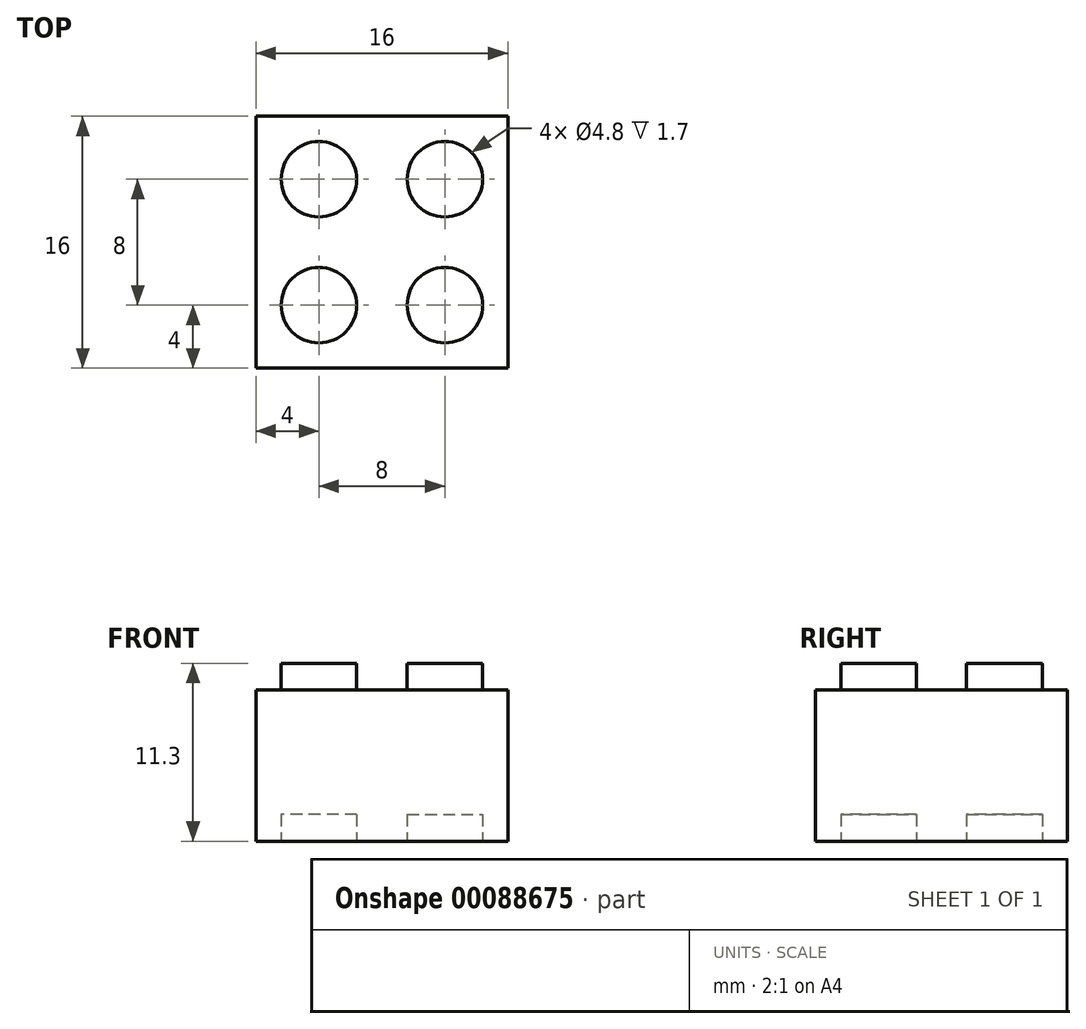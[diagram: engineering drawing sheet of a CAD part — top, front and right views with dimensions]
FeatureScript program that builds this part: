
annotation { "Feature Type Name" : "Feature", "Feature Type Description" : "" }
export const myFeature = defineFeature(function(context is Context, id is Id, definition is map)
    precondition{}
    {
        {
            var Q0;
            Q0=qCreatedBy(makeId("Front.planeOp"),FACE);
            var sketch = newSketch(context, id + "F0", { "sketchPlane" : qUnion([Q0])});
            skLineSegment(sketch, "E0.bottom", {"start": v(-4, 9.6) * mm, "end": v(-2.4, 9.6) * mm});
            skLineSegment(sketch, "E0.top", {"start": v(-4, 0) * mm, "end": v(4, 0) * mm});
            skLineSegment(sketch, "E0.left", {"start": v(-4, 9.6) * mm, "end": v(-4, 0) * mm});
            skLineSegment(sketch, "E0.right", {"start": v(4, 9.6) * mm, "end": v(4, 0) * mm});
            skLineSegment(sketch, "E1.top", {"start": v(-2.4, 11.3) * mm, "end": v(2.4, 11.3) * mm});
            skLineSegment(sketch, "E1.left", {"start": v(-2.4, 9.6) * mm, "end": v(-2.4, 11.3) * mm});
            skLineSegment(sketch, "E1.right", {"start": v(2.4, 9.6) * mm, "end": v(2.4, 11.3) * mm});
            skLineSegment(sketch, "E2", {"start": v(0, 0) * mm, "end": v(0, 24.04) * mm, "construction": true});
            skLineSegment(sketch, "E3.trimOffspring", {"start": v(2.4, 9.6) * mm, "end": v(4, 9.6) * mm});
            skSolve(sketch);
        }
        {
            var Q0;
            Q0=makeQuery(id+"F0.imprint","IMPRINT",FACE,{"disambiguationData":[TD([[makeQuery(id+"F0.imprint","IMPRINT",EDGE,{"derivedFrom":sQuery(id+"F0.wireOp",EDGE,"E0.bottom")}),-1.0]])]});
            extrude(context, id + "F1", {"entities" : qUnion([Q0]), "depth" : 8 * mm});
        }
        {
            var Q0;
            Q0=qCreatedBy(makeId("Top.planeOp"),FACE);
            var Q1;
            Q1=makeQuery(id+"F1.opExtrude","CAP_VERTEX",VERTEX,{"disambiguationData":[OSD([sQuery(id+"F0.wireOp",EDGE,"E1.top"),sQuery(id+"F0.wireOp",EDGE,"E1.right")])],"isStart":true});
            cPlane(context, id + "F2", {"entities" : qUnion([Q0, Q1]), "cplaneType" : CPlaneType.PLANE_POINT, "offset" : 152.4 * mm, "width" : 152.4 * mm, "height" : 152.4 * mm});
        }
        {
            var Q0;
            Q0=qCreatedBy(id+"F2.planeOp",FACE);
            var sketch = newSketch(context, id + "F3", { "sketchPlane" : qUnion([Q0])});
            skLineSegment(sketch, "E4.0", {"start": v(-4, -8) * mm, "end": v(-4, 0) * mm});
            skLineSegment(sketch, "E5.0", {"start": v(4, -8) * mm, "end": v(4, 0) * mm});
            skLineSegment(sketch, "E6", {"start": v(-4, 0) * mm, "end": v(4, 0) * mm});
            skLineSegment(sketch, "E7", {"start": v(-4, -8) * mm, "end": v(4, -8) * mm});
            skLineSegment(sketch, "E8", {"start": v(-4, 0) * mm, "end": v(4, -8) * mm, "construction": true});
            skLineSegment(sketch, "E9", {"start": v(-4, -8) * mm, "end": v(4, 0) * mm, "construction": true});
            skCircle(sketch, "E10", {"center": v(0, -4) * mm, "radius": 2.4 * mm});
            skSolve(sketch);
        }
        {
            var Q0;
            Q0=qSketchRegion(id+"F3",true);
            var Q1;
            Q1=makeQuery(id+"F1.opExtrude","SWEPT_FACE",FACE,{"disambiguationData":[OSD([sQuery(id+"F0.wireOp",EDGE,"E0.bottom")])]});
            extrude(context, id + "F4", {"entities" : qUnion([Q0]), "operationType" : NewBodyOperationType.REMOVE, "endBound" : BoundingType.UP_TO_SURFACE, "oppositeDirection" : true, "endBoundEntityFace" : qUnion([Q1]), "depth" : 25.4 * mm});
        }
        {
            var Q0;
            Q0=qCreatedBy(makeId("Top.planeOp"),FACE);
            var sketch = newSketch(context, id + "F5", { "sketchPlane" : qUnion([Q0])});
            skCircle(sketch, "E11.0", {"center": v(0, -4) * mm, "radius": 2.4 * mm});
            skSolve(sketch);
        }
        {
            var Q0;
            Q0=makeQuery(id+"F5.imprint","IMPRINT",FACE,{"disambiguationData":[TD([[makeQuery(id+"F5.imprint","IMPRINT",EDGE,{"derivedFrom":sQuery(id+"F5.wireOp",EDGE,"E11.0")}),1.0]])]});
            extrude(context, id + "F6", {"entities" : qUnion([Q0]), "operationType" : NewBodyOperationType.REMOVE, "depth" : 1.7 * mm});
        }
        {
            var Q0;
            Q0=qCreatedBy(makeId("Right.planeOp"),FACE);
            var Q1;
            Q1=makeQuery(id+"F1.opExtrude","CAP_VERTEX",VERTEX,{"disambiguationData":[OSD([sQuery(id+"F0.wireOp",EDGE,"E0.right"),sQuery(id+"F0.wireOp",EDGE,"E3.trimOffspring")])],"isStart":false});
            cPlane(context, id + "F7", {"entities" : qUnion([Q0, Q1]), "cplaneType" : CPlaneType.PLANE_POINT, "offset" : 152.4 * mm, "width" : 152.4 * mm, "height" : 152.4 * mm});
        }
        {
            var Q0;
            Q0=makeQuery(id+"F1.opExtrude","SWEPT_BODY",BODY,{"disambiguationData":[OSD([sQuery(id+"F0.wireOp",EDGE,"E0.bottom"),sQuery(id+"F0.wireOp",EDGE,"E0.top"),sQuery(id+"F0.wireOp",EDGE,"E0.left"),sQuery(id+"F0.wireOp",EDGE,"E0.right"),sQuery(id+"F0.wireOp",EDGE,"E1.top"),sQuery(id+"F0.wireOp",EDGE,"E1.left"),sQuery(id+"F0.wireOp",EDGE,"E1.right"),sQuery(id+"F0.wireOp",EDGE,"E3.trimOffspring")])]});
            var Q1;
            Q1=qCreatedBy(id+"F7.planeOp",FACE);
            mirror(context, id + "F8", {"operationType" : NewBodyOperationType.ADD, "entities" : qUnion([Q0]), "mirrorPlane" : qUnion([Q1])});
        }
        {
            var Q0;
            Q0=makeQuery(id+"F1.opExtrude","SWEPT_BODY",BODY,{"disambiguationData":[OSD([sQuery(id+"F0.wireOp",EDGE,"E0.bottom"),sQuery(id+"F0.wireOp",EDGE,"E0.top"),sQuery(id+"F0.wireOp",EDGE,"E0.left"),sQuery(id+"F0.wireOp",EDGE,"E0.right"),sQuery(id+"F0.wireOp",EDGE,"E1.top"),sQuery(id+"F0.wireOp",EDGE,"E1.left"),sQuery(id+"F0.wireOp",EDGE,"E1.right"),sQuery(id+"F0.wireOp",EDGE,"E3.trimOffspring")])]});
            var Q1;
            Q1=qCreatedBy(makeId("Front.planeOp"),FACE);
            mirror(context, id + "F9", {"operationType" : NewBodyOperationType.ADD, "entities" : qUnion([Q0]), "mirrorPlane" : qUnion([Q1])});
        }
    });
